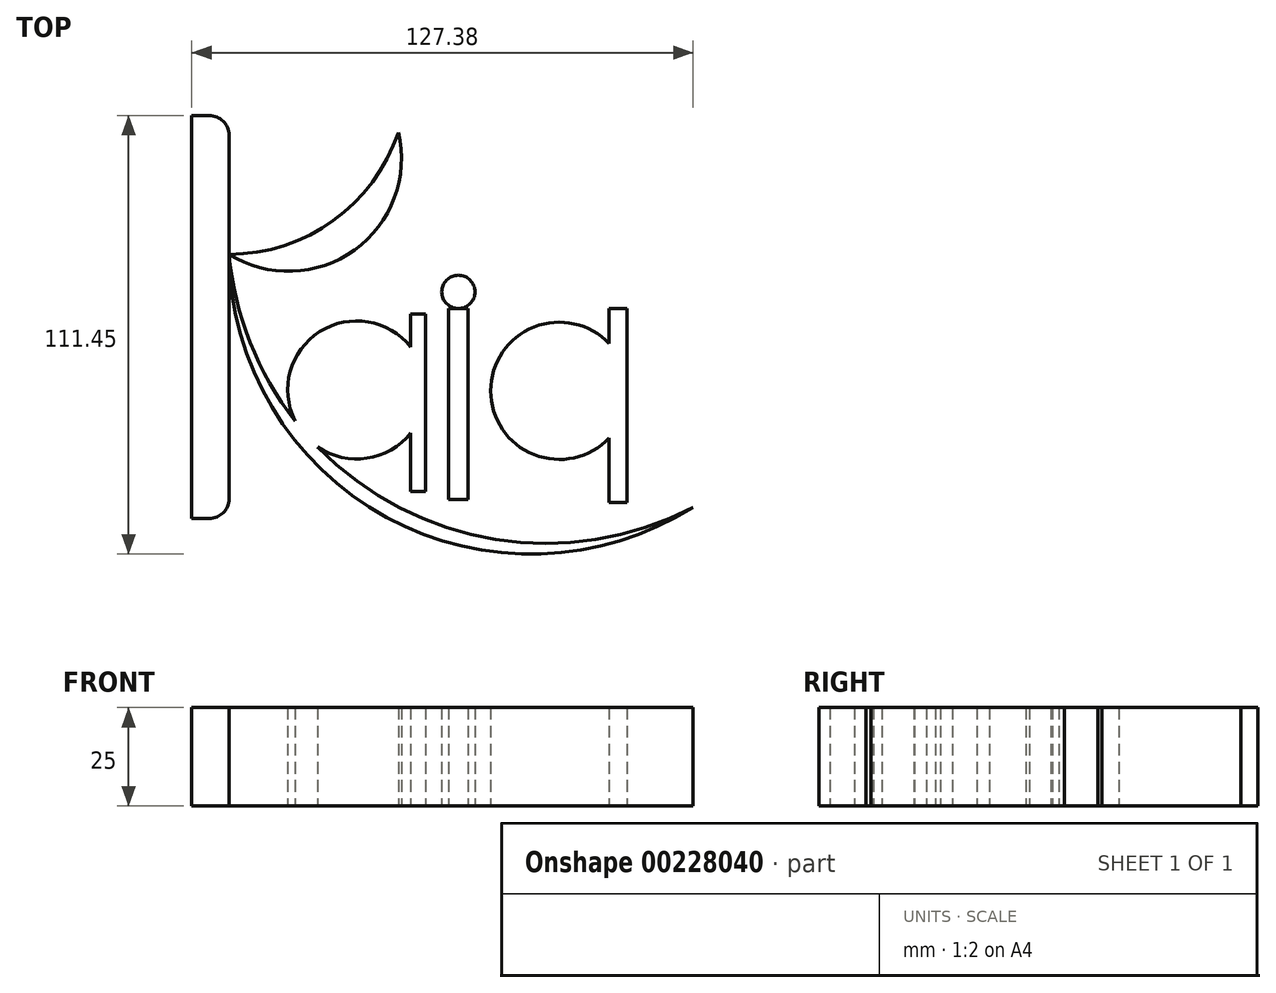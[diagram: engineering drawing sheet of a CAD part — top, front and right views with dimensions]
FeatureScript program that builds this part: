
annotation { "Feature Type Name" : "Feature", "Feature Type Description" : "" }
export const myFeature = defineFeature(function(context is Context, id is Id, definition is map)
    precondition{}
    {
        {
            var Q0;
            Q0=qCreatedBy(makeId("Top.planeOp"),FACE);
            var sketch = newSketch(context, id + "F0", { "sketchPlane" : qUnion([Q0])});
            skLineSegment(sketch, "E0.bottom", {"start": v(-73.73, 54.65) * mm, "end": v(-69.26, 54.65) * mm});
            skLineSegment(sketch, "E0.top", {"start": v(-73.73, -47.77) * mm, "end": v(-69.26, -47.77) * mm});
            skLineSegment(sketch, "E0.left", {"start": v(-73.73, 54.65) * mm, "end": v(-73.73, -47.77) * mm});
            skLineSegment(sketch, "E0.right", {"start": v(-64.26, 49.65) * mm, "end": v(-64.26, -42.77) * mm});
            skPoint(sketch, "E1.visualSharp", {"position": v(-64.26, 54.65) * mm});
            skArc(sketch, "E1.filletArc", {"start": v(-64.26, 49.65) * mm, "mid": v(-65.73, 53.19) * mm, "end": v(-69.26, 54.65) * mm});
            skPoint(sketch, "E2.visualSharp", {"position": v(-64.26, -47.77) * mm});
            skArc(sketch, "E2.filletArc", {"start": v(-69.26, -47.77) * mm, "mid": v(-65.73, -46.3) * mm, "end": v(-64.26, -42.77) * mm});
            skSolve(sketch);
        }
        {
            var Q0;
            Q0=qCreatedBy(makeId("Top.planeOp"),FACE);
            var sketch = newSketch(context, id + "F1", { "sketchPlane" : qUnion([Q0])});
            skArc(sketch, "E3", {"start": v(-64.26, 19.36) * mm, "mid": v(-32.38, 20.46) * mm, "end": v(-21.23, 50.35) * mm});
            skArc(sketch, "E4", {"start": v(-64.26, 19.36) * mm, "mid": v(-37.75, 27.92) * mm, "end": v(-21.23, 50.35) * mm});
            skArc(sketch, "E5", {"start": v(-64.26, 19.36) * mm, "mid": v(-24.2, -47.43) * mm, "end": v(53.65, -44.9) * mm});
            skArc(sketch, "E6", {"start": v(-64.26, 19.36) * mm, "mid": v(-22.43, -44.19) * mm, "end": v(53.65, -44.9) * mm});
            skSolve(sketch);
        }
        {
            var Q0;
            Q0=qCreatedBy(makeId("Top.planeOp"),FACE);
            var sketch = newSketch(context, id + "F2", { "sketchPlane" : qUnion([Q0])});
            skCircle(sketch, "E7", {"center": v(-31.8, -15.09) * mm, "radius": 17.54 * mm});
            skPoint(sketch, "E7.first.point", {"position": v(-40.74, 0) * mm});
            skPoint(sketch, "E7.second.point", {"position": v(-24.1, -30.84) * mm});
            skPoint(sketch, "E7.third.point", {"position": v(-35.29, -32.27) * mm});
            skLineSegment(sketch, "E8.bottom", {"start": v(-18.07, 4.16) * mm, "end": v(-14.34, 4.16) * mm});
            skLineSegment(sketch, "E8.top", {"start": v(-18.07, -40.88) * mm, "end": v(-14.34, -40.88) * mm});
            skLineSegment(sketch, "E8.left", {"start": v(-18.07, 4.16) * mm, "end": v(-18.07, -40.88) * mm});
            skLineSegment(sketch, "E8.right", {"start": v(-14.34, 4.16) * mm, "end": v(-14.34, -40.88) * mm});
            skSolve(sketch);
        }
        {
            var Q0;
            Q0=qCreatedBy(makeId("Top.planeOp"),FACE);
            var sketch = newSketch(context, id + "F3", { "sketchPlane" : qUnion([Q0])});
            skLineSegment(sketch, "E9.bottom", {"start": v(-8.46, 5.6) * mm, "end": v(-3.48, 5.6) * mm});
            skLineSegment(sketch, "E9.top", {"start": v(-8.46, -42.92) * mm, "end": v(-3.48, -42.92) * mm});
            skLineSegment(sketch, "E9.left", {"start": v(-8.46, 5.6) * mm, "end": v(-8.46, -42.92) * mm});
            skLineSegment(sketch, "E9.right", {"start": v(-3.48, 5.6) * mm, "end": v(-3.48, -42.92) * mm});
            skCircle(sketch, "E10", {"center": v(-5.97, 9.83) * mm, "radius": 4.23 * mm});
            skPoint(sketch, "E10.centerSnap0", {"position": v(-5.97, 5.6) * mm});
            skCircle(sketch, "E11", {"center": v(19.66, -15.3) * mm, "radius": 17.44 * mm});
            skLineSegment(sketch, "E12.bottom", {"start": v(32.35, 5.6) * mm, "end": v(36.82, 5.6) * mm});
            skLineSegment(sketch, "E12.top", {"start": v(32.35, -43.67) * mm, "end": v(36.82, -43.67) * mm});
            skLineSegment(sketch, "E12.left", {"start": v(32.35, 5.6) * mm, "end": v(32.35, -43.67) * mm});
            skLineSegment(sketch, "E12.right", {"start": v(36.82, 5.6) * mm, "end": v(36.82, -43.67) * mm});
            skSolve(sketch);
        }
        {
            var Q0;
            Q0=makeQuery(id+"F3.imprint","IMPRINT",FACE,{"disambiguationData":[TD([[makeQuery(id+"F3.imprint","IMPRINT",EDGE,{"derivedFrom":sQuery(id+"F3.wireOp",EDGE,"E9.top")}),1.0]])]});
            var Q1;
            Q1=makeQuery(id+"F3.imprint","IMPRINT",FACE,{"disambiguationData":[TD([[makeQuery(id+"F3.imprint","IMPRINT",EDGE,{"derivedFrom":sQuery(id+"F3.wireOp",EDGE,"E10")}),1.0]])]});
            var Q2;
            {var subQ5=sQuery(id+"F3.wireOp",EDGE,"E12.bottom");Q2=makeQuery(id+"F3.imprint","IMPRINT",FACE,{"disambiguationData":[TD([[makeQuery(id+"F3.imprint","IMPRINT",EDGE,{"derivedFrom":subQ5}),-1.0]])]});}
            var Q3;
            {var subQ5=sQuery(id+"F3.wireOp",EDGE,"E12.top");Q3=makeQuery(id+"F3.imprint","IMPRINT",FACE,{"disambiguationData":[TD([[makeQuery(id+"F3.imprint","IMPRINT",EDGE,{"derivedFrom":subQ5}),1.0]])]});}
            var Q4;
            {var subQ0=sQuery(id+"F3.wireOp",EDGE,"E12.right");var subQ1=sQuery(id+"F3.wireOp",EDGE,"E11");var subQ2=makeQuery(id+"F3.imprint","INTERSECT",VERTEX,{"disambiguationData":[OD(0.0)],"derivedFrom":[subQ1,subQ0]});Q4=makeQuery(id+"F3.imprint","IMPRINT",FACE,{"disambiguationData":[TD([[makeQuery(id+"F3.imprint","IMPRINT",EDGE,{"disambiguationData":[TD([[subQ2,1.0]])],"derivedFrom":subQ1}),1.0]])]});}
            var Q5;
            {var subQ0=sQuery(id+"F3.wireOp",EDGE,"E12.left");var subQ1=sQuery(id+"F3.wireOp",EDGE,"E11");var subQ2=makeQuery(id+"F3.imprint","INTERSECT",VERTEX,{"disambiguationData":[OD(0.0)],"derivedFrom":[subQ1,subQ0]});Q5=makeQuery(id+"F3.imprint","IMPRINT",FACE,{"disambiguationData":[TD([[makeQuery(id+"F3.imprint","IMPRINT",EDGE,{"disambiguationData":[TD([[subQ2,1.0]])],"derivedFrom":subQ1}),1.0]])]});}
            var Q6;
            {var subQ0=sQuery(id+"F3.wireOp",EDGE,"E12.left");var subQ1=sQuery(id+"F3.wireOp",EDGE,"E11");var subQ2=makeQuery(id+"F3.imprint","INTERSECT",VERTEX,{"disambiguationData":[OD(0.0)],"derivedFrom":[subQ1,subQ0]});Q6=makeQuery(id+"F3.imprint","IMPRINT",FACE,{"disambiguationData":[TD([[makeQuery(id+"F3.imprint","IMPRINT",EDGE,{"disambiguationData":[TD([[subQ2,-1.0]])],"derivedFrom":subQ1}),1.0]])]});}
            extrude(context, id + "F4", {"entities" : qUnion([Q0, Q1, Q2, Q3, Q4, Q5, Q6]), "depth" : 25 * mm});
        }
        {
            var Q0;
            Q0 = qSketchRegion(id + "F2", true);
            extrude(context, id + "F5", {"entities" : qUnion([Q0]), "depth" : 25 * mm});
        }
        {
            var Q0;
            Q0 = qSketchRegion(id + "F1", true);
            extrude(context, id + "F6", {"entities" : qUnion([Q0]), "operationType" : NewBodyOperationType.ADD, "depth" : 25 * mm});
        }
        {
            var Q0;
            Q0 = qSketchRegion(id + "F0", true);
            extrude(context, id + "F7", {"entities" : qUnion([Q0]), "depth" : 25 * mm});
        }
    });
